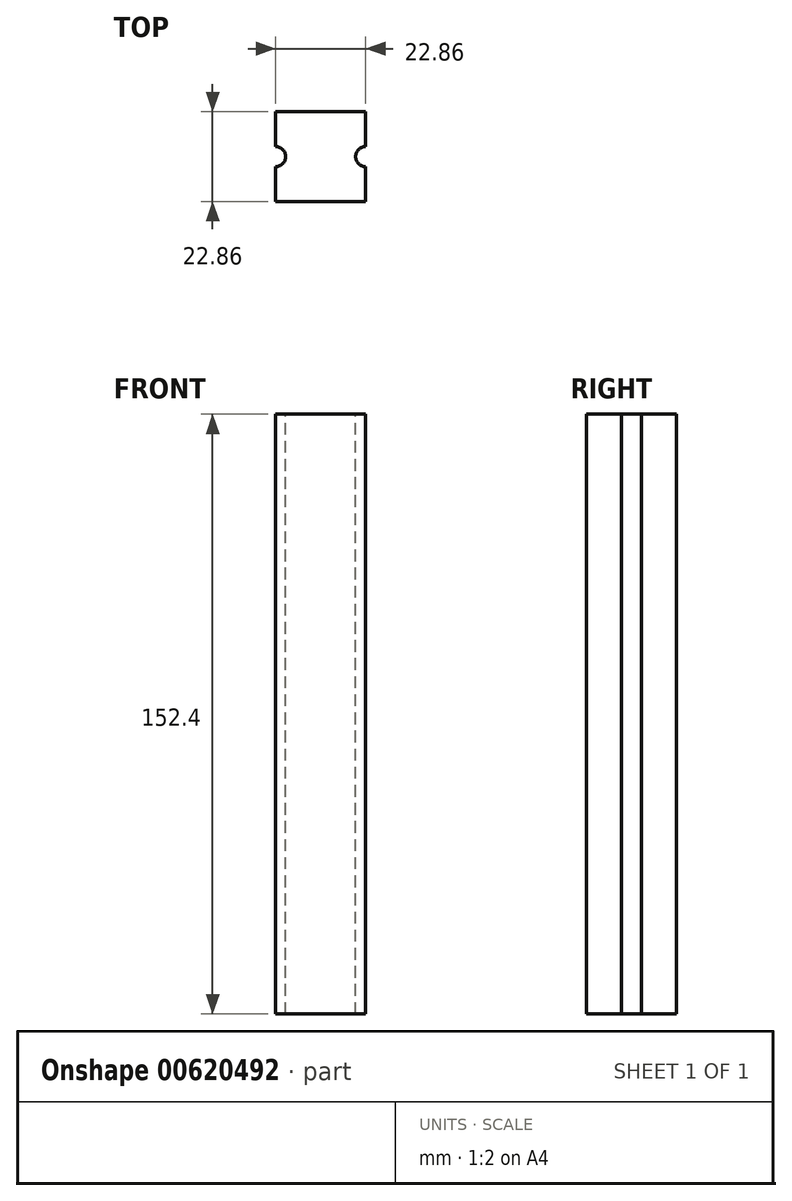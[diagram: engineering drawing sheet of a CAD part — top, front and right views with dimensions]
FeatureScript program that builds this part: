
annotation { "Feature Type Name" : "Feature", "Feature Type Description" : "" }
export const myFeature = defineFeature(function(context is Context, id is Id, definition is map)
    precondition{}
    {
        {
            var Q0;
            Q0=qCreatedBy(makeId("Right.planeOp"),FACE);
            var sketch = newSketch(context, id + "F0", { "sketchPlane" : qUnion([Q0])});
            skLineSegment(sketch, "E0.bottom", {"start": v(-22.91, 122.56) * mm, "end": v(-0.05, 122.56) * mm});
            skLineSegment(sketch, "E0.top", {"start": v(-22.91, -29.84) * mm, "end": v(-0.05, -29.84) * mm});
            skLineSegment(sketch, "E0.left", {"start": v(-22.91, 122.56) * mm, "end": v(-22.91, -29.84) * mm});
            skLineSegment(sketch, "E0.right", {"start": v(-0.05, 122.56) * mm, "end": v(-0.05, -29.84) * mm});
            skSolve(sketch);
        }
        {
            var Q0;
            Q0=makeQuery(id+"F0.imprint","IMPRINT",FACE,{"disambiguationData":[TD([[makeQuery(id+"F0.imprint","IMPRINT",EDGE,{"derivedFrom":sQuery(id+"F0.wireOp",EDGE,"E0.bottom")}),-1.0]])]});
            extrude(context, id + "F1", {"entities" : qUnion([Q0]), "depth" : 22.86 * mm, "offsetDistance" : 25.4 * mm});
        }
        {
            var Q0;
            Q0=makeQuery(id+"F1.opExtrude","SWEPT_FACE",FACE,{"disambiguationData":[OSD([sQuery(id+"F0.wireOp",EDGE,"E0.bottom")])]});
            var sketch = newSketch(context, id + "F2", { "sketchPlane" : qUnion([Q0])});
            skCircle(sketch, "E1", {"center": v(22.86, -11.48) * mm, "radius": 2.54 * mm});
            skCircle(sketch, "E2", {"center": v(0, -11.48) * mm, "radius": 2.54 * mm});
            skSolve(sketch);
        }
        {
            var Q0;
            {var subQ0=sQuery(id+"F2.wireOp",EDGE,"E1");var subQ1=makeQuery(id+"F1.opExtrude","CAP_EDGE",EDGE,{"disambiguationData":[OSD([sQuery(id+"F0.wireOp",EDGE,"E0.bottom")])],"isStart":false});var subQ2=makeQuery(id+"F2.imprint","INTERSECT",VERTEX,{"disambiguationData":[OD(0.0)],"derivedFrom":[subQ1,subQ0]});Q0=makeQuery(id+"F2.imprint","IMPRINT",FACE,{"disambiguationData":[TD([[makeQuery(id+"F2.imprint","IMPRINT",EDGE,{"disambiguationData":[TD([[subQ2,-1.0]])],"derivedFrom":subQ0}),1.0]])]});}
            var Q1;
            {var subQ0=sQuery(id+"F2.wireOp",EDGE,"E2");var subQ1=makeQuery(id+"F1.opExtrude","CAP_EDGE",EDGE,{"disambiguationData":[OSD([sQuery(id+"F0.wireOp",EDGE,"E0.bottom")])],"isStart":true});var subQ2=makeQuery(id+"F2.imprint","INTERSECT",VERTEX,{"disambiguationData":[OD(0.0)],"derivedFrom":[subQ1,subQ0]});Q1=makeQuery(id+"F2.imprint","IMPRINT",FACE,{"disambiguationData":[TD([[makeQuery(id+"F2.imprint","IMPRINT",EDGE,{"disambiguationData":[TD([[subQ2,1.0]])],"derivedFrom":subQ0}),1.0]])]});}
            var Q2;
            {var subQ0=sQuery(id+"F2.wireOp",EDGE,"E1");var subQ1=makeQuery(id+"F1.opExtrude","CAP_EDGE",EDGE,{"disambiguationData":[OSD([sQuery(id+"F0.wireOp",EDGE,"E0.bottom")])],"isStart":false});var subQ2=makeQuery(id+"F2.imprint","INTERSECT",VERTEX,{"disambiguationData":[OD(0.0)],"derivedFrom":[subQ1,subQ0]});Q2=makeQuery(id+"F2.imprint","IMPRINT",FACE,{"disambiguationData":[TD([[makeQuery(id+"F2.imprint","IMPRINT",EDGE,{"disambiguationData":[TD([[subQ2,1.0]])],"derivedFrom":subQ0}),1.0]])]});}
            extrude(context, id + "F3", {"entities" : qUnion([Q0, Q1, Q2]), "operationType" : NewBodyOperationType.REMOVE, "oppositeDirection" : true, "depth" : 152.4 * mm, "offsetDistance" : 25.4 * mm});
        }
        {
            var Q0;
            Q0=makeQuery(id+"F1.opExtrude","SWEPT_FACE",FACE,{"disambiguationData":[OSD([sQuery(id+"F0.wireOp",EDGE,"E0.bottom")])]});
            var sketch = newSketch(context, id + "F4", { "sketchPlane" : qUnion([Q0])});
            skCircle(sketch, "E3", {"center": v(0, -11.48) * mm, "radius": 2.54 * mm});
            skSolve(sketch);
        }
        {
            var Q0;
            {var subQ0=sQuery(id+"F4.wireOp",EDGE,"E3");var subQ1=makeQuery(id+"F1.opExtrude","CAP_EDGE",EDGE,{"disambiguationData":[OSD([sQuery(id+"F0.wireOp",EDGE,"E0.bottom")])],"isStart":true});var subQ2=makeQuery(id+"F4.imprint","INTERSECT",VERTEX,{"disambiguationData":[OD(0.0)],"derivedFrom":[subQ1,subQ0]});Q0=makeQuery(id+"F4.imprint","IMPRINT",FACE,{"disambiguationData":[TD([[makeQuery(id+"F4.imprint","IMPRINT",EDGE,{"disambiguationData":[TD([[subQ2,-1.0]])],"derivedFrom":subQ0}),1.0]])]});}
            extrude(context, id + "F5", {"entities" : qUnion([Q0]), "operationType" : NewBodyOperationType.REMOVE, "oppositeDirection" : true, "depth" : 152.4 * mm, "offsetDistance" : 25.4 * mm});
        }
    });
